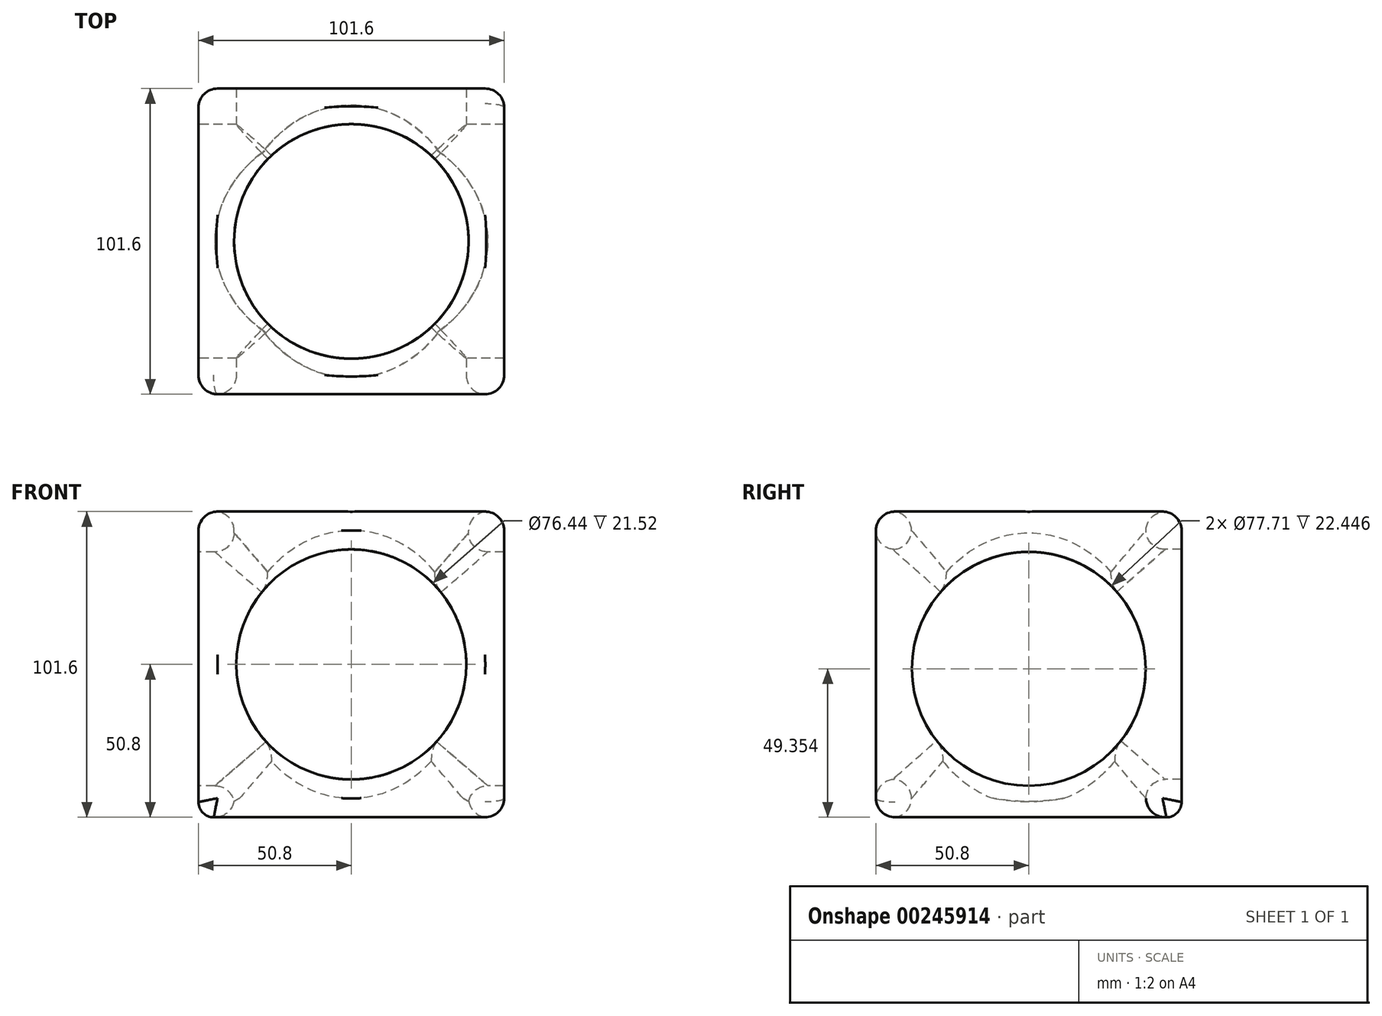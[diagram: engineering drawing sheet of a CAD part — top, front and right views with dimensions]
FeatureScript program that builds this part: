
annotation { "Feature Type Name" : "Feature", "Feature Type Description" : "" }
export const myFeature = defineFeature(function(context is Context, id is Id, definition is map)
    precondition{}
    {
        {
            var Q0;
            Q0=qCreatedBy(makeId("Front.planeOp"),FACE);
            var sketch = newSketch(context, id + "F0", { "sketchPlane" : qUnion([Q0])});
            skLineSegment(sketch, "E0", {"start": v(0, 0) * mm, "end": v(101.6, 0) * mm});
            skPoint(sketch, "E1.start.orphan", {"position": v(101.6, -3.95) * mm});
            skPoint(sketch, "E2.start.orphan", {"position": v(107.36, 0) * mm});
            skPoint(sketch, "E3.end.orphan", {"position": v(107.36, 38.23) * mm});
            skPoint(sketch, "E4.start.orphan", {"position": v(110.91, 50.52) * mm});
            skLineSegment(sketch, "E5", {"start": v(0, 101.6) * mm, "end": v(0, 0) * mm});
            skPoint(sketch, "E6.start.orphan", {"position": v(107.36, 50.52) * mm});
            skLineSegment(sketch, "E7", {"start": v(87.63, 0) * mm, "end": v(101.6, 0) * mm});
            skPoint(sketch, "E8.end.orphan", {"position": v(87.63, 88.04) * mm});
            skLineSegment(sketch, "E9", {"start": v(0, 101.6) * mm, "end": v(101.6, 101.6) * mm});
            skPoint(sketch, "E10.end.orphan", {"position": v(87.63, 83.28) * mm});
            skPoint(sketch, "E10.start.orphan", {"position": v(87.63, 52.5) * mm});
            skLineSegment(sketch, "E11", {"start": v(101.6, 101.6) * mm, "end": v(101.6, 4.34) * mm});
            skLineSegment(sketch, "E12", {"start": v(101.6, 4.34) * mm, "end": v(101.6, -7.5) * mm});
            skSolve(sketch);
        }
        {
            var Q0;
            Q0=makeQuery(id+"F0.imprint","IMPRINT",FACE,{"disambiguationData":[TD([[makeQuery(id+"F0.imprint","IMPRINT",EDGE,{"derivedFrom":sQuery(id+"F0.wireOp",EDGE,"E0")}),1.0]])]});
            extrude(context, id + "F1", {"entities" : qUnion([Q0]), "depth" : 101.6 * mm});
        }
        {
            var Q0;
            Q0=makeQuery(id+"F1.opExtrude","CAP_FACE",FACE,{"disambiguationData":[OSD([sQuery(id+"F0.wireOp",EDGE,"E0"),sQuery(id+"F0.wireOp",EDGE,"E5"),sQuery(id+"F0.wireOp",EDGE,"E7"),sQuery(id+"F0.wireOp",EDGE,"E9"),sQuery(id+"F0.wireOp",EDGE,"E11"),sQuery(id+"F0.wireOp",EDGE,"E12")])],"isStart":false});
            var sketch = newSketch(context, id + "F2", { "sketchPlane" : qUnion([Q0])});
            skCircle(sketch, "E13", {"center": v(50.8, 50.8) * mm, "radius": 38.22 * mm});
            skSolve(sketch);
        }
        {
            var Q0;
            Q0=makeQuery(id+"F2.imprint","IMPRINT",FACE,{"disambiguationData":[TD([[makeQuery(id+"F2.imprint","IMPRINT",EDGE,{"derivedFrom":sQuery(id+"F2.wireOp",EDGE,"E13")}),1.0]])]});
            extrude(context, id + "F3", {"entities" : qUnion([Q0]), "operationType" : NewBodyOperationType.REMOVE, "oppositeDirection" : true, "depth" : 101.6 * mm});
        }
        {
            var Q0;
            Q0=makeQuery(id+"F1.opExtrude","SWEPT_FACE",FACE,{"disambiguationData":[OSD([sQuery(id+"F0.wireOp",EDGE,"E5")])]});
            var sketch = newSketch(context, id + "F4", { "sketchPlane" : qUnion([Q0])});
            skCircle(sketch, "E14", {"center": v(50.8, 49.35) * mm, "radius": 38.86 * mm});
            skPoint(sketch, "E15.orphan", {"position": v(50.8, 101.6) * mm});
            skPoint(sketch, "E16.end.orphan", {"position": v(50.8, -2.9) * mm});
            skSolve(sketch);
        }
        {
            var Q0;
            Q0=makeQuery(id+"F4.imprint","IMPRINT",FACE,{"disambiguationData":[TD([[makeQuery(id+"F4.imprint","IMPRINT",EDGE,{"derivedFrom":sQuery(id+"F4.wireOp",EDGE,"E14")}),1.0]])]});
            extrude(context, id + "F5", {"entities" : qUnion([Q0]), "operationType" : NewBodyOperationType.REMOVE, "oppositeDirection" : true, "depth" : 101.6 * mm});
        }
        {
            var Q0;
            Q0=makeQuery(id+"F1.opExtrude","SWEPT_FACE",FACE,{"disambiguationData":[OSD([sQuery(id+"F0.wireOp",EDGE,"E9")])]});
            var sketch = newSketch(context, id + "F6", { "sketchPlane" : qUnion([Q0])});
            skPoint(sketch, "E17.endSnap0", {"position": v(50.8, -101.6) * mm});
            skPoint(sketch, "E18.start.orphan", {"position": v(50.8, 0) * mm});
            skPoint(sketch, "E17.end.orphan", {"position": v(50.8, -110.55) * mm});
            skLineSegment(sketch, "E19", {"start": v(50.8, 0) * mm, "end": v(50.8, -101.6) * mm});
            skCircle(sketch, "E20", {"center": v(50.8, -50.8) * mm, "radius": 38.97 * mm});
            skSolve(sketch);
        }
        {
            var Q0;
            Q0 = qSketchRegion(id + "F6", true);
            extrude(context, id + "F7", {"entities" : qUnion([Q0]), "operationType" : NewBodyOperationType.REMOVE, "oppositeDirection" : true, "depth" : 101.6 * mm});
        }
        {
            var Q0;
            Q0=makeQuery(id+"F1.opExtrude","SWEPT_EDGE",EDGE,{"disambiguationData":[OSD([sQuery(id+"F0.wireOp",EDGE,"E9"),sQuery(id+"F0.wireOp",EDGE,"E11")])]});
            var Q1;
            Q1=makeQuery(id+"F1.opExtrude","CAP_EDGE",EDGE,{"disambiguationData":[OSD([sQuery(id+"F0.wireOp",EDGE,"E11"),sQuery(id+"F0.wireOp",EDGE,"E12")])],"isStart":true});
            var Q2;
            Q2=makeQuery(id+"F1.opExtrude","CAP_EDGE",EDGE,{"disambiguationData":[OSD([sQuery(id+"F0.wireOp",EDGE,"E9")])],"isStart":true});
            var Q3;
            Q3=makeQuery(id+"F1.opExtrude","SWEPT_EDGE",EDGE,{"disambiguationData":[OSD([sQuery(id+"F0.wireOp",EDGE,"E5"),sQuery(id+"F0.wireOp",EDGE,"E9")])]});
            var Q4;
            Q4=makeQuery(id+"F1.opExtrude","CAP_EDGE",EDGE,{"disambiguationData":[OSD([sQuery(id+"F0.wireOp",EDGE,"E9")])],"isStart":false});
            var Q5;
            Q5=makeQuery(id+"F1.opExtrude","CAP_EDGE",EDGE,{"disambiguationData":[OSD([sQuery(id+"F0.wireOp",EDGE,"E5")])],"isStart":false});
            var Q6;
            Q6=makeQuery(id+"F1.opExtrude","CAP_EDGE",EDGE,{"disambiguationData":[OSD([sQuery(id+"F0.wireOp",EDGE,"E0"),sQuery(id+"F0.wireOp",EDGE,"E7")])],"isStart":false});
            var Q7;
            Q7=makeQuery(id+"F1.opExtrude","CAP_FACE",FACE,{"disambiguationData":[OSD([sQuery(id+"F0.wireOp",EDGE,"E0"),sQuery(id+"F0.wireOp",EDGE,"E5"),sQuery(id+"F0.wireOp",EDGE,"E7"),sQuery(id+"F0.wireOp",EDGE,"E9"),sQuery(id+"F0.wireOp",EDGE,"E11"),sQuery(id+"F0.wireOp",EDGE,"E12")])],"isStart":false});
            var Q8;
            Q8=makeQuery(id+"F1.opExtrude","SWEPT_EDGE",EDGE,{"disambiguationData":[OSD([sQuery(id+"F0.wireOp",EDGE,"E7"),sQuery(id+"F0.wireOp",EDGE,"E12")])]});
            var Q9;
            Q9=makeQuery(id+"F7.boolean.opBoolean","COPY",FACE,{"disambiguationData":[TD([makeQuery(id+"F1.opExtrude","SWEPT_FACE",FACE,{"disambiguationData":[OSD([sQuery(id+"F0.wireOp",EDGE,"E9")])]})])],"derivedFrom":makeQuery(id+"F7.opExtrude","SWEPT_FACE",FACE,{"disambiguationData":[OSD([sQuery(id+"F6.wireOp",EDGE,"E20")])]})});
            var Q10;
            Q10=makeQuery(id+"F3.boolean.opBoolean","COPY",EDGE,{"derivedFrom":makeQuery(id+"F3.opExtrude","CAP_EDGE",EDGE,{"disambiguationData":[OSD([sQuery(id+"F2.wireOp",EDGE,"E13")])],"isStart":false})});
            var Q11;
            Q11=makeQuery(id+"F7.boolean.opBoolean","INTERSECT",EDGE,{"disambiguationData":[OD(3.0)],"derivedFrom":[makeQuery(id+"F5.boolean.opBoolean","COPY",FACE,{"derivedFrom":makeQuery(id+"F5.opExtrude","SWEPT_FACE",FACE,{"disambiguationData":[OSD([sQuery(id+"F4.wireOp",EDGE,"E14")])]})}),makeQuery(id+"F7.opExtrude","SWEPT_FACE",FACE,{"disambiguationData":[OSD([sQuery(id+"F6.wireOp",EDGE,"E20")])]})]});
            var Q12;
            Q12=makeQuery(id+"F5.boolean.opBoolean","COPY",EDGE,{"derivedFrom":makeQuery(id+"F5.opExtrude","CAP_EDGE",EDGE,{"disambiguationData":[OSD([sQuery(id+"F4.wireOp",EDGE,"E14")])],"isStart":true})});
            var Q13;
            Q13=makeQuery(id+"F7.boolean.opBoolean","COPY",FACE,{"disambiguationData":[TD([makeQuery(id+"F1.opExtrude","SWEPT_FACE",FACE,{"disambiguationData":[OSD([sQuery(id+"F0.wireOp",EDGE,"E0"),sQuery(id+"F0.wireOp",EDGE,"E7")])]})])],"derivedFrom":makeQuery(id+"F7.opExtrude","SWEPT_FACE",FACE,{"disambiguationData":[OSD([sQuery(id+"F6.wireOp",EDGE,"E20")])]})});
            var Q14;
            Q14=makeQuery(id+"F5.boolean.opBoolean","COPY",EDGE,{"derivedFrom":makeQuery(id+"F5.opExtrude","CAP_EDGE",EDGE,{"disambiguationData":[OSD([sQuery(id+"F4.wireOp",EDGE,"E14")])],"isStart":false})});
            fillet(context, id + "F8", {"entities" : qUnion([Q0, Q1, Q2, Q3, Q4, Q5, Q6, Q7, Q8, Q9, Q10, Q11, Q12, Q13, Q14]), "radius" : 6.35 * mm, "tangentPropagation" : true, "allowEdgeOverflow" : false});
        }
        {
            var Q0;
            Q0=makeQuery(id+"F1.opExtrude","CAP_EDGE",EDGE,{"disambiguationData":[OSD([sQuery(id+"F0.wireOp",EDGE,"E0"),sQuery(id+"F0.wireOp",EDGE,"E7")])],"isStart":true});
            var Q1;
            Q1=makeQuery(id+"F1.opExtrude","SWEPT_EDGE",EDGE,{"disambiguationData":[OSD([sQuery(id+"F0.wireOp",EDGE,"E0"),sQuery(id+"F0.wireOp",EDGE,"E5")])]});
            fillet(context, id + "F9", {"entities" : qUnion([Q0, Q1]), "radius" : 5.08 * mm, "tangentPropagation" : true, "allowEdgeOverflow" : false});
        }
        {
            var Q0;
            Q0=makeQuery(id+"F1.opExtrude","CAP_EDGE",EDGE,{"disambiguationData":[OSD([sQuery(id+"F0.wireOp",EDGE,"E5")])],"isStart":true});
            fillet(context, id + "F10", {"entities" : qUnion([Q0]), "radius" : 6.35 * mm, "tangentPropagation" : true, "allowEdgeOverflow" : false});
        }
    });
